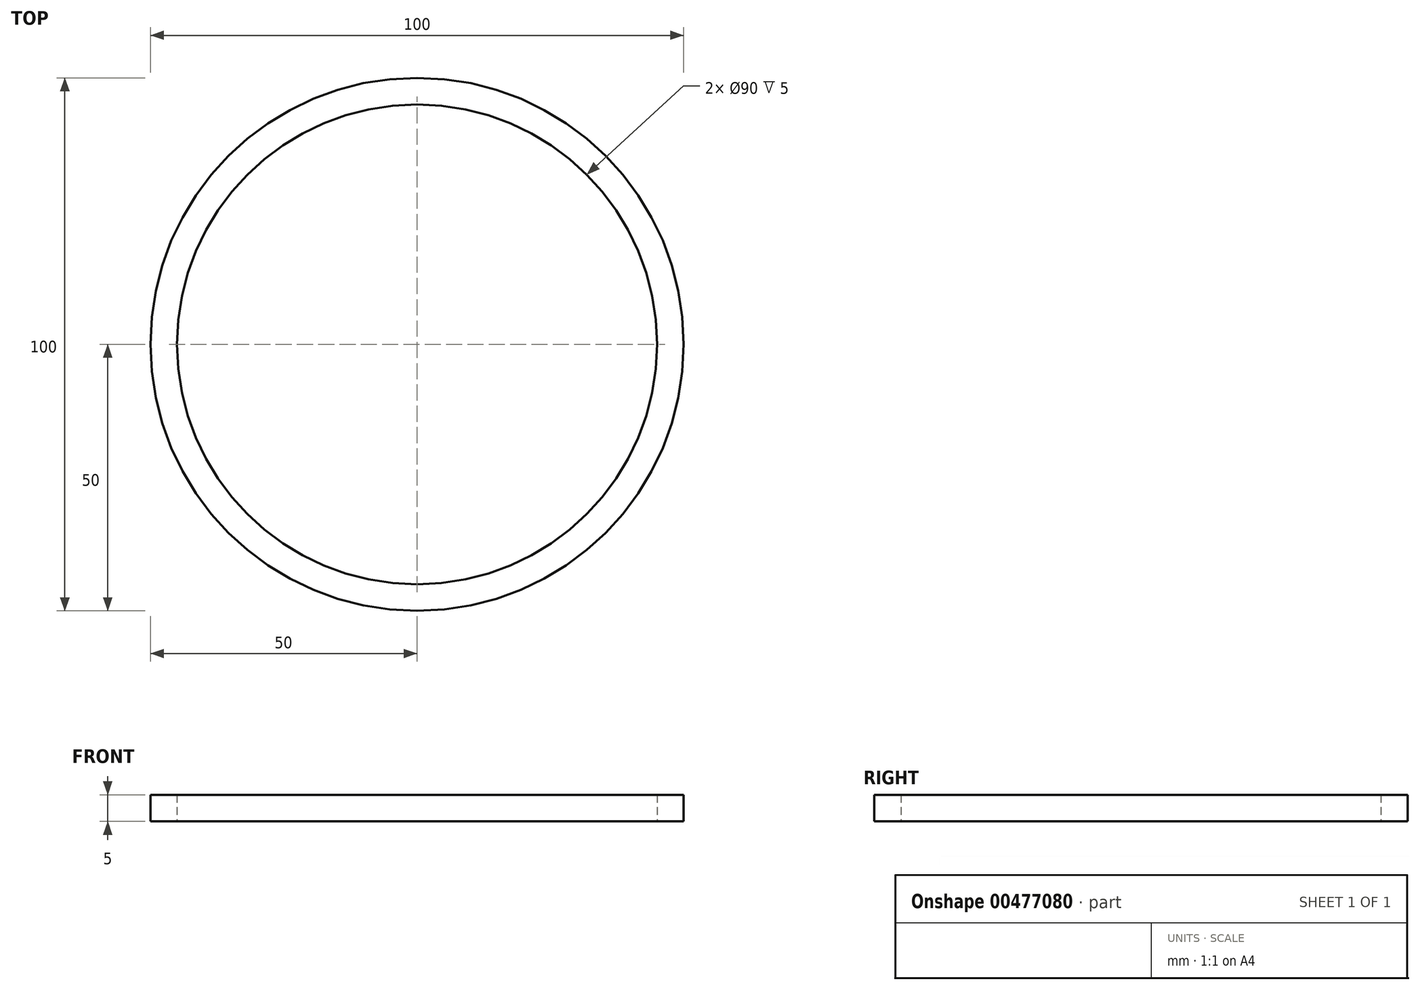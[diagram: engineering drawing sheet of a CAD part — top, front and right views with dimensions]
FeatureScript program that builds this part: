
annotation { "Feature Type Name" : "Feature", "Feature Type Description" : "" }
export const myFeature = defineFeature(function(context is Context, id is Id, definition is map)
    precondition{}
    {
        {
            var Q0;
            Q0=qCreatedBy(makeId("Top.planeOp"),FACE);
            var sketch = newSketch(context, id + "F0", { "sketchPlane" : qUnion([Q0])});
            skCircle(sketch, "E0", {"center": v(0, 0) * mm, "radius": 50 * mm});
            skSolve(sketch);
        }
        {
            var Q0;
            Q0=qCreatedBy(makeId("Top.planeOp"),FACE);
            var sketch = newSketch(context, id + "F1", { "sketchPlane" : qUnion([Q0])});
            skCircle(sketch, "E1", {"center": v(0, 0) * mm, "radius": 45 * mm});
            skSolve(sketch);
        }
        {
            var Q0;
            Q0=makeQuery(id+"F0.imprint","IMPRINT",FACE,{"disambiguationData":[TD([[makeQuery(id+"F0.imprint","IMPRINT",EDGE,{"derivedFrom":sQuery(id+"F0.wireOp",EDGE,"E0")}),1.0]])]});
            var Q1;
            Q1=sQuery(id+"F0.wireOp",EDGE,"E0");
            extrude(context, id + "F2", {"entities" : qUnion([Q0]), "surfaceEntities" : qUnion([Q1]), "depth" : 5 * mm, "offsetDistance" : 25 * mm});
        }
        {
            var Q0;
            Q0 = qSketchRegion(id + "F1", true);
            extrude(context, id + "F3", {"entities" : qUnion([Q0]), "operationType" : NewBodyOperationType.REMOVE, "endBound" : BoundingType.THROUGH_ALL, "depth" : 25 * mm, "offsetDistance" : 25 * mm});
        }
        {
            var Q0;
            Q0=makeQuery(id+"F2.opExtrude","SWEPT_BODY",BODY,{"disambiguationData":[OSD([sQuery(id+"F0.wireOp",EDGE,"E0")])]});
            transform(context, id + "F4", {"entities" : qUnion([Q0]), "transformType" : TransformType.TRANSLATION_3D, "dx" : 0 * mm, "dy" : 0 * mm, "dz" : 0 * mm, "makeCopy" : true});
        }
    });
